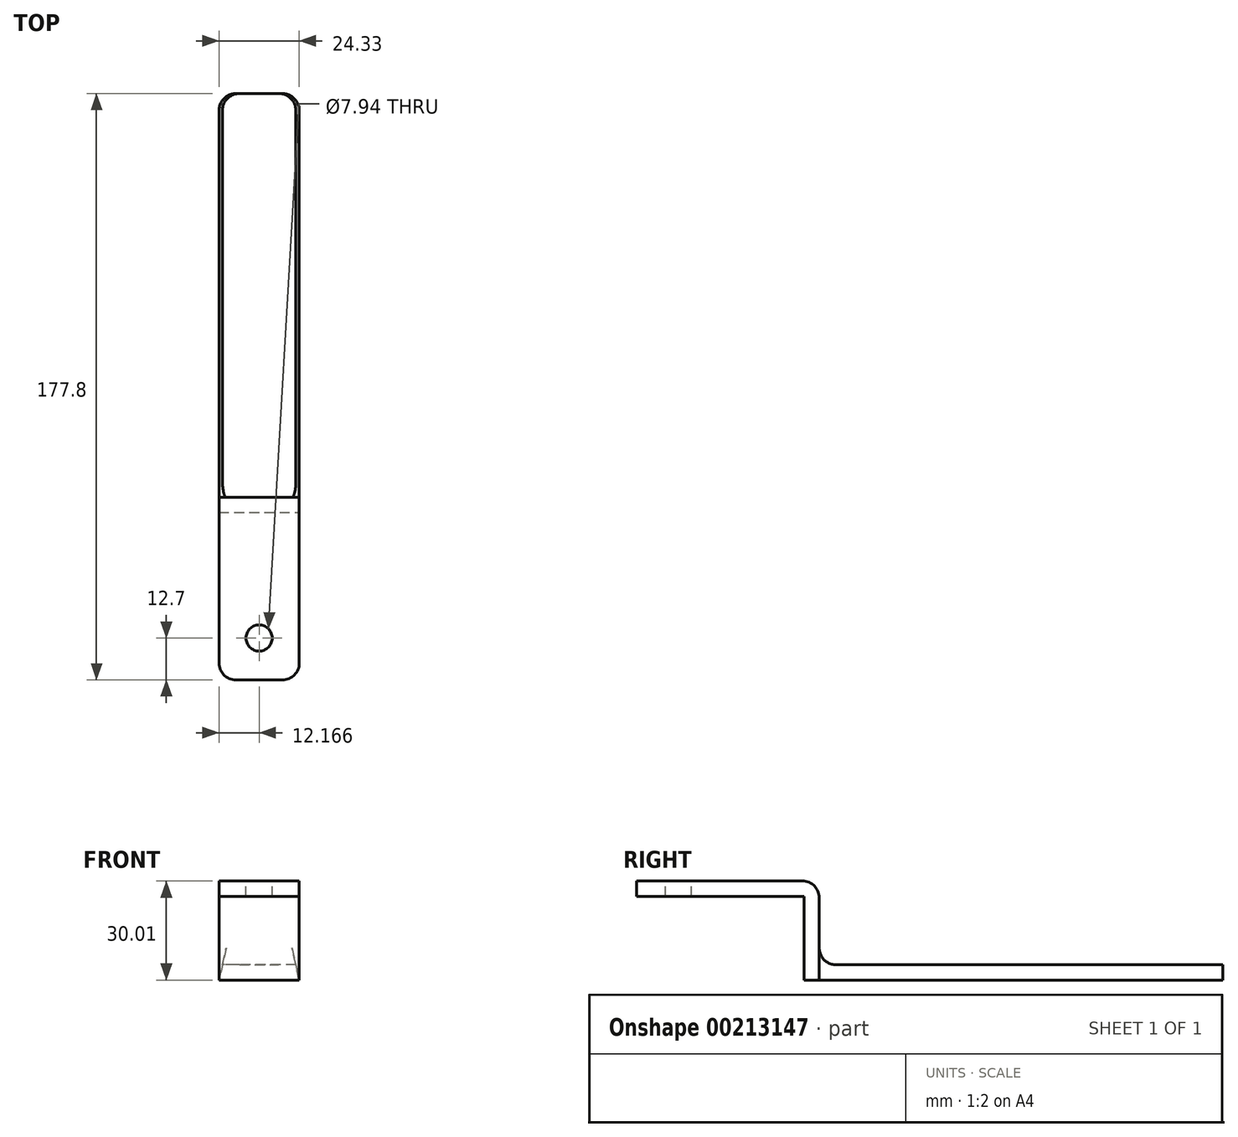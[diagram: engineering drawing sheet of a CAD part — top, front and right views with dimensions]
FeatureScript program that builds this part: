
annotation { "Feature Type Name" : "Feature", "Feature Type Description" : "" }
export const myFeature = defineFeature(function(context is Context, id is Id, definition is map)
    precondition{}
    {
        {
            var Q0;
            Q0=qCreatedBy(makeId("Front.planeOp"),FACE);
            var sketch = newSketch(context, id + "F0", { "sketchPlane" : qUnion([Q0])});
            skLineSegment(sketch, "E0", {"start": v(0, 0) * mm, "end": v(25.97, 0) * mm});
            skLineSegment(sketch, "E1", {"start": v(25.97, 0) * mm, "end": v(24.94, 4.61) * mm, "construction": true});
            skLineSegment(sketch, "E2", {"start": v(24.94, 4.61) * mm, "end": v(1.03, 4.61) * mm, "construction": true});
            skLineSegment(sketch, "E3", {"start": v(1.03, 4.61) * mm, "end": v(0, 0) * mm, "construction": true});
            skLineSegment(sketch, "E4.0", {"start": v(25.15, 0) * mm, "end": v(24.12, 4.61) * mm});
            skLineSegment(sketch, "E5", {"start": v(12.99, 4.61) * mm, "end": v(12.99, 0) * mm, "construction": true});
            skLineSegment(sketch, "E6.MirrorCS", {"start": v(0.82, 0) * mm, "end": v(1.85, 4.61) * mm});
            skLineSegment(sketch, "E7", {"start": v(1.85, 4.61) * mm, "end": v(24.12, 4.61) * mm});
            skLineSegment(sketch, "E8", {"start": v(25.15, 0) * mm, "end": v(0.82, 0) * mm});
            skSolve(sketch);
        }
        {
            var Q0;
            Q0 = qSketchRegion(id + "F0", true);
            extrude(context, id + "F1", {"entities" : qUnion([Q0]), "depth" : 127 * mm});
        }
        {
            var Q0;
            Q0=makeQuery(id+"F1.opExtrude","SWEPT_FACE",FACE,{"disambiguationData":[OSD([sQuery(id+"F0.wireOp",EDGE,"E7")])]});
            var sketch = newSketch(context, id + "F2", { "sketchPlane" : qUnion([Q0])});
            skLineSegment(sketch, "E9.0", {"start": v(0.82, -127) * mm, "end": v(0.82, 0) * mm});
            skLineSegment(sketch, "E10.0", {"start": v(25.15, -127) * mm, "end": v(25.15, 0) * mm});
            skLineSegment(sketch, "E11.0.0", {"start": v(1.85, 0) * mm, "end": v(0.82, 0) * mm, "construction": true});
            skLineSegment(sketch, "E11.0.1", {"start": v(0.82, 0) * mm, "end": v(0.82, -127) * mm, "construction": true});
            skLineSegment(sketch, "E12.0.0", {"start": v(25.15, 0) * mm, "end": v(24.12, 0) * mm, "construction": true});
            skLineSegment(sketch, "E12.0.3", {"start": v(25.15, -127) * mm, "end": v(25.15, 0) * mm, "construction": true});
            skLineSegment(sketch, "E13.bottom", {"start": v(0.82, -127) * mm, "end": v(25.15, -127) * mm});
            skLineSegment(sketch, "E13.top", {"start": v(0.82, -122.39) * mm, "end": v(25.15, -122.39) * mm});
            skLineSegment(sketch, "E13.left", {"start": v(0.82, -127) * mm, "end": v(0.82, -122.39) * mm});
            skLineSegment(sketch, "E13.right", {"start": v(25.15, -127) * mm, "end": v(25.15, -122.39) * mm});
            skSolve(sketch);
        }
        {
            var Q0;
            Q0 = qSketchRegion(id + "F2", true);
            extrude(context, id + "F3", {"entities" : qUnion([Q0]), "operationType" : NewBodyOperationType.ADD, "depth" : 25.4 * mm, "hasSecondDirection" : true, "secondDirectionOppositeDirection" : true, "secondDirectionDepth" : 4.61 * mm});
        }
        {
            var Q0;
            Q0=makeQuery(id+"F3.boolean.opBoolean","MERGE",FACE,{"derivedFrom":[makeQuery(id+"F1.opExtrude","CAP_FACE",FACE,{"disambiguationData":[OSD([sQuery(id+"F0.wireOp",EDGE,"E4.0"),sQuery(id+"F0.wireOp",EDGE,"E6.MirrorCS"),sQuery(id+"F0.wireOp",EDGE,"E7"),sQuery(id+"F0.wireOp",EDGE,"E8")])],"isStart":false}),makeQuery(id+"F3.opExtrude","SWEPT_FACE",FACE,{"disambiguationData":[OSD([sQuery(id+"F2.wireOp",EDGE,"E13.bottom")])]})]});
            var sketch = newSketch(context, id + "F4", { "sketchPlane" : qUnion([Q0])});
            skLineSegment(sketch, "E14.bottom", {"start": v(0.82, 30.01) * mm, "end": v(25.15, 30.01) * mm});
            skLineSegment(sketch, "E14.top", {"start": v(0.82, 25.4) * mm, "end": v(25.15, 25.4) * mm});
            skLineSegment(sketch, "E14.left", {"start": v(0.82, 30.01) * mm, "end": v(0.82, 25.4) * mm});
            skLineSegment(sketch, "E14.right", {"start": v(25.15, 30.01) * mm, "end": v(25.15, 25.4) * mm});
            skSolve(sketch);
        }
        {
            var Q0;
            Q0 = qSketchRegion(id + "F4", true);
            extrude(context, id + "F5", {"entities" : qUnion([Q0]), "operationType" : NewBodyOperationType.ADD, "depth" : 50.8 * mm});
        }
        {
            var Q0;
            Q0=makeQuery(id+"F3.boolean.opBoolean","INTERSECT",EDGE,{"derivedFrom":[makeQuery(id+"F1.opExtrude","SWEPT_FACE",FACE,{"disambiguationData":[OSD([sQuery(id+"F0.wireOp",EDGE,"E7")])]}),makeQuery(id+"F3.opExtrude","SWEPT_FACE",FACE,{"disambiguationData":[OSD([sQuery(id+"F2.wireOp",EDGE,"E13.top")])]})]});
            var Q1;
            Q1=makeQuery(id+"F3.opExtrude","CAP_EDGE",EDGE,{"disambiguationData":[OSD([sQuery(id+"F2.wireOp",EDGE,"E13.top")])],"isStart":false});
            var Q2;
            Q2=makeQuery(id+"F1.opExtrude","CAP_EDGE",EDGE,{"disambiguationData":[OSD([sQuery(id+"F0.wireOp",EDGE,"E8")])],"isStart":false});
            var Q3;
            Q3=makeQuery(id+"F5.opExtrude","CAP_EDGE",EDGE,{"disambiguationData":[OSD([sQuery(id+"F4.wireOp",EDGE,"E14.top")])],"isStart":true});
            var Q4;
            Q4=makeQuery(id+"F5.opExtrude","CAP_EDGE",EDGE,{"disambiguationData":[OSD([sQuery(id+"F4.wireOp",EDGE,"E14.left")])],"isStart":false});
            var Q5;
            Q5=makeQuery(id+"F5.opExtrude","CAP_EDGE",EDGE,{"disambiguationData":[OSD([sQuery(id+"F4.wireOp",EDGE,"E14.right")])],"isStart":false});
            var Q6;
            Q6=makeQuery(id+"F1.opExtrude","CAP_EDGE",EDGE,{"disambiguationData":[OSD([sQuery(id+"F0.wireOp",EDGE,"E6.MirrorCS")])],"isStart":true});
            var Q7;
            Q7=makeQuery(id+"F1.opExtrude","CAP_EDGE",EDGE,{"disambiguationData":[OSD([sQuery(id+"F0.wireOp",EDGE,"E4.0")])],"isStart":true});
            fillet(context, id + "F6", {"entities" : qUnion([Q0, Q1, Q2, Q3, Q4, Q5, Q6, Q7]), "radius" : 5.08 * mm, "tangentPropagation" : true, "allowEdgeOverflow" : false});
        }
        {
            var Q0;
            Q0=makeQuery(id+"F5.boolean.opBoolean","MERGE",FACE,{"derivedFrom":[makeQuery(id+"F3.opExtrude","CAP_FACE",FACE,{"disambiguationData":[OSD([sQuery(id+"F2.wireOp",EDGE,"E13.bottom"),sQuery(id+"F2.wireOp",EDGE,"E13.top"),sQuery(id+"F2.wireOp",EDGE,"E13.left"),sQuery(id+"F2.wireOp",EDGE,"E13.right")])],"isStart":false}),makeQuery(id+"F5.opExtrude","SWEPT_FACE",FACE,{"disambiguationData":[OSD([sQuery(id+"F4.wireOp",EDGE,"E14.bottom")])]})]});
            var sketch = newSketch(context, id + "F7", { "sketchPlane" : qUnion([Q0])});
            skLineSegment(sketch, "E15", {"start": v(12.99, -127.47) * mm, "end": v(12.99, -177.8) * mm});
            skPoint(sketch, "E16", {"position": v(12.99, -165.1) * mm});
            skSolve(sketch);
        }
        {
            var Q0;
            Q0=sQuery(id+"F7.wireOp",VERTEX,"E16");
            var Q1;
            Q1=makeQuery(id+"F1.opExtrude","SWEPT_BODY",BODY,{"disambiguationData":[OSD([sQuery(id+"F0.wireOp",EDGE,"E4.0"),sQuery(id+"F0.wireOp",EDGE,"E6.MirrorCS"),sQuery(id+"F0.wireOp",EDGE,"E7"),sQuery(id+"F0.wireOp",EDGE,"E8")])]});
            hole(context, id + "F8", {"style" : HoleStyle.SIMPLE, "endStyle" : HoleEndStyle.BLIND, "holeDiameter" : 7.94 * mm, "holeDepth" : 19.05 * mm, "startFromSketch" : true, "locations" : qUnion([Q0]), "scope" : qUnion([Q1])});
        }
    });
